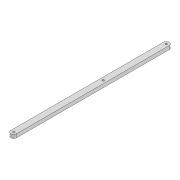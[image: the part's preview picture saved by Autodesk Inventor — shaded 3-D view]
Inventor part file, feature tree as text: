
AUTODESK INVENTOR PART (.ipt)
format: ipt  version: 2022 (Build 260153000, 153)  size: 89,600 bytes
history: native  units: mm
features: extrude x1, sketch x1
ambient origin geometry x8: Origin, YZ Plane, XZ Plane, XY Plane, X Axis, Y Axis, Z Axis, Center Point
bodies: Solid1 (feature_tree)
feature tree (2):
  extrude  "Extrusion1"  Depth=6.0mm
  sketch  "Sketch1"  dims[d0=3.3mm d1=3.3mm d2=10.0mm d3=261.6mm d4=3.3mm d5=153.559mm d6=6.0mm d7=0.0mm]
